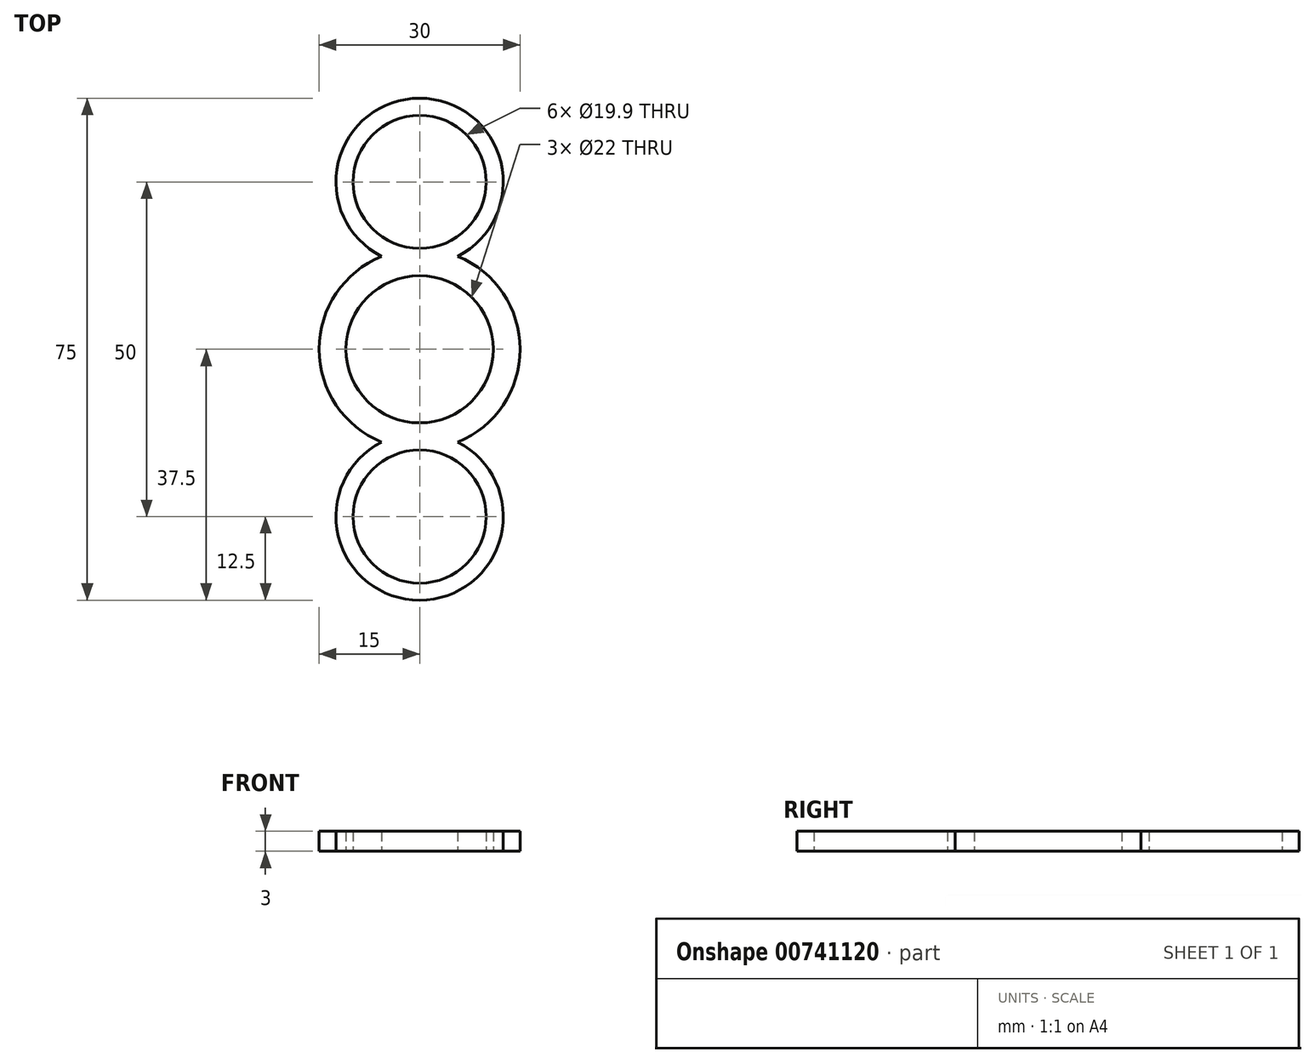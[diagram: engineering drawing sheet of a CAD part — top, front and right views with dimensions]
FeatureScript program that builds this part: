
annotation { "Feature Type Name" : "Feature", "Feature Type Description" : "" }
export const myFeature = defineFeature(function(context is Context, id is Id, definition is map)
    precondition{}
    {
        {
            var Q0;
            Q0=qCreatedBy(makeId("Top.planeOp"),FACE);
            var sketch = newSketch(context, id + "F0", { "sketchPlane" : qUnion([Q0])});
            skArc(sketch, "E0", {"start": v(11, 0) * mm, "mid": v(0, 11) * mm, "end": v(-11, 0) * mm});
            skCircle(sketch, "E1", {"center": v(0, 25) * mm, "radius": 9.95 * mm});
            skArc(sketch, "E2", {"start": v(-5.7, 13.87) * mm, "mid": v(-12.46, 8.35) * mm, "end": v(-15, 0) * mm});
            skArc(sketch, "E3", {"start": v(5.7, 13.88) * mm, "mid": v(0, 37.5) * mm, "end": v(-5.7, 13.88) * mm});
            skArc(sketch, "E4.trimOffspring", {"start": v(15, 0) * mm, "mid": v(12.46, 8.35) * mm, "end": v(5.7, 13.87) * mm});
            skCircle(sketch, "E5.1.0", {"center": v(0, -25) * mm, "radius": 9.95 * mm});
            skArc(sketch, "E5.1.1", {"start": v(-5.7, -13.88) * mm, "mid": v(0, -37.5) * mm, "end": v(5.7, -13.88) * mm});
            skArc(sketch, "E5.1.2", {"start": v(-15, 0) * mm, "mid": v(-12.46, -8.35) * mm, "end": v(-5.7, -13.87) * mm});
            skArc(sketch, "E5.1.3", {"start": v(-11, 0) * mm, "mid": v(0, -11) * mm, "end": v(11, 0) * mm});
            skArc(sketch, "E5.1.4", {"start": v(5.7, -13.87) * mm, "mid": v(12.46, -8.35) * mm, "end": v(15, 0) * mm});
            skSolve(sketch);
        }
        {
            var Q0;
            Q0 = qSketchRegion(id + "F0", true);
            extrude(context, id + "F1", {"entities" : qUnion([Q0]), "depth" : 3 * mm, "offsetDistance" : 25 * mm});
        }
    });
